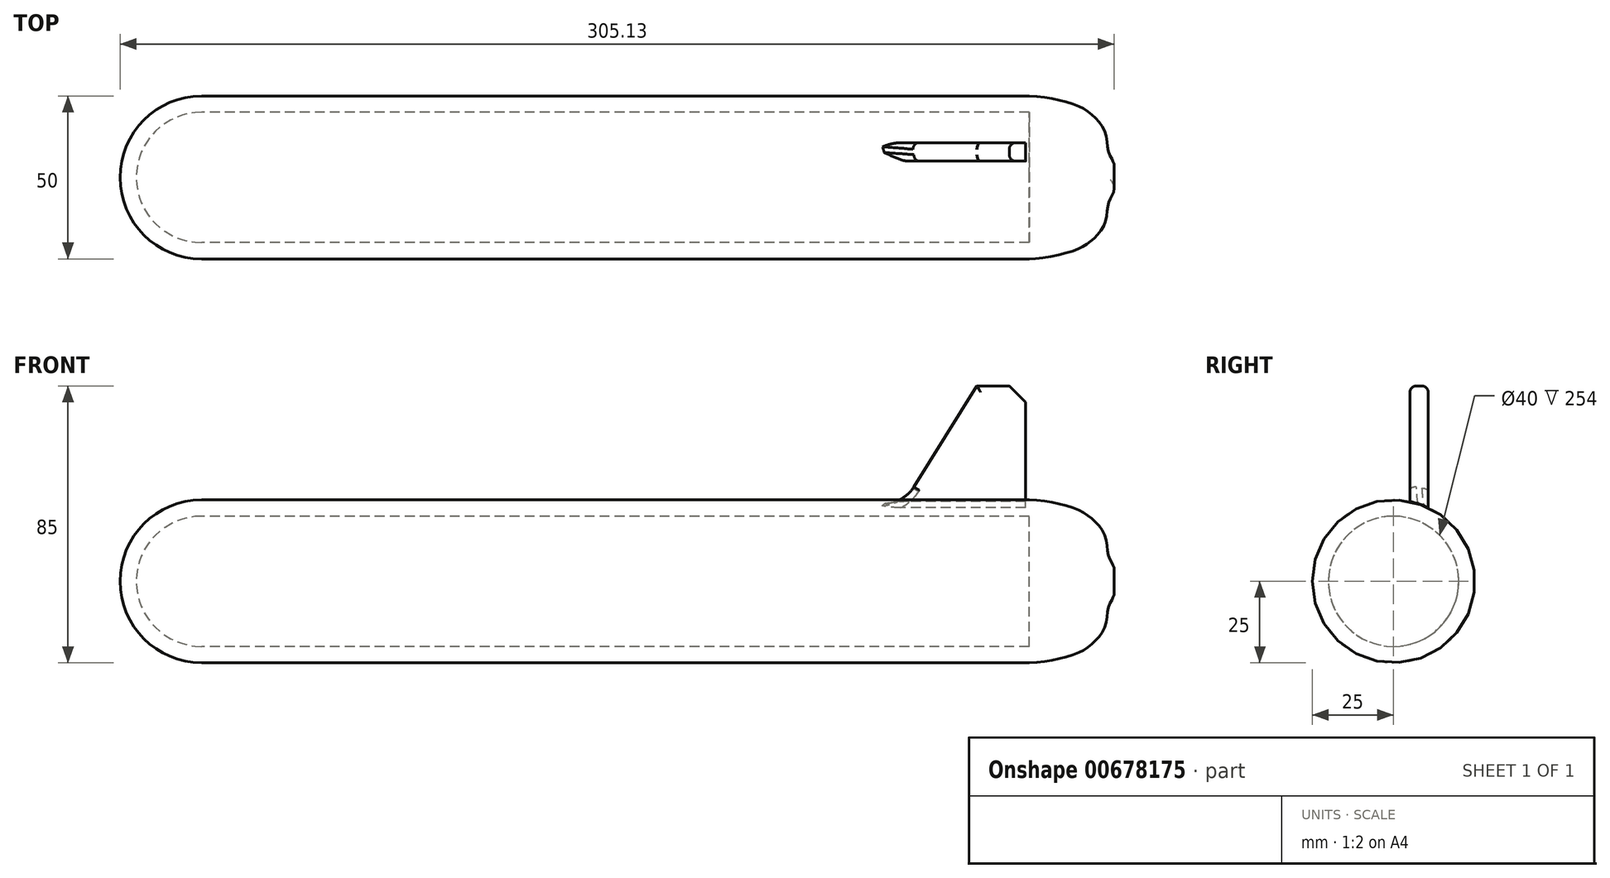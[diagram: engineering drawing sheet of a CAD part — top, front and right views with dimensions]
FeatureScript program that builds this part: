
annotation { "Feature Type Name" : "Feature", "Feature Type Description" : "" }
export const myFeature = defineFeature(function(context is Context, id is Id, definition is map)
    precondition{}
    {
        {
            var Q0;
            Q0=qCreatedBy(makeId("Right.planeOp"),FACE);
            var sketch = newSketch(context, id + "F0", { "sketchPlane" : qUnion([Q0])});
            skCircle(sketch, "E0", {"center": v(0, 0) * mm, "radius": 25 * mm});
            skCircle(sketch, "E1", {"center": v(0, 0) * mm, "radius": 20 * mm});
            skSolve(sketch);
        }
        {
            var Q0;
            Q0=makeQuery(id+"F0.imprint","IMPRINT",FACE,{"disambiguationData":[TD([[makeQuery(id+"F0.imprint","IMPRINT",EDGE,{"derivedFrom":sQuery(id+"F0.wireOp",EDGE,"E0")}),1.0]])]});
            extrude(context, id + "F1", {"entities" : qUnion([Q0]), "endBound" : BoundingType.SYMMETRIC, "depth" : 254 * mm, "offsetDistance" : 25 * mm});
        }
        {
            var Q0;
            Q0=makeQuery(id+"F1.opExtrude","CAP_FACE",FACE,{"disambiguationData":[OSD([sQuery(id+"F0.wireOp",EDGE,"E0"),sQuery(id+"F0.wireOp",EDGE,"E1")])],"isStart":true});
            var sketch = newSketch(context, id + "F2", { "sketchPlane" : qUnion([Q0])});
            skLineSegment(sketch, "E2", {"start": v(0, 46.44) * mm, "end": v(0, -46.44) * mm, "construction": true});
            skArc(sketch, "E3", {"start": v(0, -25) * mm, "mid": v(25, 0) * mm, "end": v(0, 25) * mm});
            skArc(sketch, "E4", {"start": v(0, -20) * mm, "mid": v(20, 0) * mm, "end": v(0, 20) * mm});
            skLineSegment(sketch, "E5", {"start": v(0, 25) * mm, "end": v(0, 20) * mm});
            skLineSegment(sketch, "E6", {"start": v(0, -20) * mm, "end": v(0, -25) * mm});
            skSolve(sketch);
        }
        {
            var Q0;
            Q0=makeQuery(id+"F2.imprint","IMPRINT",FACE,{"disambiguationData":[TD([[makeQuery(id+"F2.imprint","IMPRINT",EDGE,{"derivedFrom":sQuery(id+"F2.wireOp",EDGE,"E3")}),-1.0]])]});
            var Q1;
            Q1=sQuery(id+"F2.wireOp",EDGE,"E2");
            revolve(context, id + "F3", {"operationType" : NewBodyOperationType.ADD, "entities" : qUnion([Q0]), "axis" : qUnion([Q1]), "revolveType" : RevolveType.ONE_DIRECTION, "angle" : 180 * degree});
        }
        {
            var Q0;
            Q0=qCreatedBy(makeId("Top.planeOp"),FACE);
            var sketch = newSketch(context, id + "F4", { "sketchPlane" : qUnion([Q0])});
            skFitSpline(sketch, "E7.MirrorCS", {"points": [v(127, -25) * mm, v(140.66, -22.5) * mm, v(146.09, -19.4) * mm, v(150.23, -14.19) * mm, v(151.3, -8.12) * mm, v(152.86, -4.69) * mm, v(151.36, 0) * mm], "startDerivative": vector(46.37, -0.27) * mm, "endDerivative": vector(-41.82, 42.97) * mm});
            skLineSegment(sketch, "E8", {"start": v(0, 0) * mm, "end": v(187.94, 0) * mm, "construction": true});
            skLineSegment(sketch, "E9", {"start": v(151.36, 0) * mm, "end": v(127, 0) * mm});
            skLineSegment(sketch, "E10", {"start": v(127, -25) * mm, "end": v(127, 0) * mm});
            skSolve(sketch);
        }
        {
            var Q0;
            Q0=makeQuery(id+"F4.imprint","IMPRINT",FACE,{"disambiguationData":[TD([[makeQuery(id+"F4.imprint","IMPRINT",EDGE,{"derivedFrom":sQuery(id+"F4.wireOp",EDGE,"E7.MirrorCS")}),1.0]])]});
            var Q1;
            Q1=sQuery(id+"F4.wireOp",EDGE,"E8");
            revolve(context, id + "F5", {"operationType" : NewBodyOperationType.ADD, "entities" : qUnion([Q0]), "axis" : qUnion([Q1]), "revolveType" : RevolveType.FULL});
        }
        {
            var Q0;
            Q0=qCreatedBy(makeId("Top.planeOp"),FACE);
            cPlane(context, id + "F6", {"entities" : qUnion([Q0]), "cplaneType" : CPlaneType.OFFSET, "offset" : 60 * mm, "width" : 150 * mm, "height" : 150 * mm});
        }
        {
            var Q0;
            Q0=qCreatedBy(id+"F6.planeOp",FACE);
            var sketch = newSketch(context, id + "F7", { "sketchPlane" : qUnion([Q0])});
            skLineSegment(sketch, "E11.bottom", {"start": v(125.91, 5) * mm, "end": v(86, 5) * mm});
            skLineSegment(sketch, "E11.top", {"start": v(125.91, 10.65) * mm, "end": v(86, 10.65) * mm});
            skLineSegment(sketch, "E11.left", {"start": v(125.91, 5) * mm, "end": v(125.91, 10.65) * mm});
            skLineSegment(sketch, "E11.right", {"start": v(86, 5) * mm, "end": v(86, 10.65) * mm});
            skPoint(sketch, "E11.middle", {"position": v(105.96, 7.82) * mm});
            skSolve(sketch);
        }
        {
            var Q0;
            Q0=makeQuery(id+"F7.imprint","IMPRINT",FACE,{"disambiguationData":[TD([[makeQuery(id+"F7.imprint","IMPRINT",EDGE,{"derivedFrom":sQuery(id+"F7.wireOp",EDGE,"E11.bottom")}),-1.0]])]});
            var Q1;
            Q1=makeQuery(id+"F1.opExtrude","SWEPT_FACE",FACE,{"disambiguationData":[OSD([sQuery(id+"F0.wireOp",EDGE,"E0")])]});
            extrude(context, id + "F8", {"entities" : qUnion([Q0]), "operationType" : NewBodyOperationType.ADD, "endBound" : BoundingType.UP_TO_SURFACE, "oppositeDirection" : true, "depth" : 25 * mm, "endBoundEntityFace" : qUnion([Q1]), "offsetDistance" : 25 * mm});
        }
        {
            var Q0;
            Q0=makeQuery(id+"F8.opExtrude","CAP_EDGE",EDGE,{"disambiguationData":[OSD([sQuery(id+"F7.wireOp",EDGE,"E11.left")])],"isStart":true});
            chamfer(context, id + "F9", {"entities" : qUnion([Q0]), "width" : 5 * mm, "tangentPropagation" : true});
        }
        {
            var Q0;
            Q0=makeQuery(id+"F8.opExtrude","CAP_EDGE",EDGE,{"disambiguationData":[OSD([sQuery(id+"F7.wireOp",EDGE,"E11.right")])],"isStart":true});
            chamfer(context, id + "F10", {"entities" : qUnion([Q0]), "chamferType" : ChamferType.TWO_OFFSETS, "width1" : 40 * mm, "oppositeDirection" : false, "width2" : 25 * mm, "tangentPropagation" : true});
        }
        {
            var Q0;
            {var subQ0=sQuery(id+"F7.wireOp",EDGE,"E11.right");Q0=makeQuery(id+"F10.opChamfer","BLEND_EDGE",EDGE,{"blendedFrom":[makeQuery(id+"F8.opExtrude","CAP_EDGE",EDGE,{"disambiguationData":[OSD([subQ0])],"isStart":true}),makeQuery(id+"F8.opExtrude","CAP_FACE",FACE,{"disambiguationData":[OSD([sQuery(id+"F7.wireOp",EDGE,"E11.bottom"),sQuery(id+"F7.wireOp",EDGE,"E11.top"),sQuery(id+"F7.wireOp",EDGE,"E11.left"),subQ0])],"isStart":true})],"blendedInto":[makeQuery(id+"F8.opExtrude","CAP_FACE",FACE,{"disambiguationData":[OSD([sQuery(id+"F7.wireOp",EDGE,"E11.bottom"),sQuery(id+"F7.wireOp",EDGE,"E11.top"),sQuery(id+"F7.wireOp",EDGE,"E11.left"),subQ0])],"isStart":true})]});}
            var Q1;
            {var subQ0=sQuery(id+"F7.wireOp",EDGE,"E11.left");Q1=makeQuery(id+"F9.opChamfer","BLEND_EDGE",EDGE,{"blendedFrom":[makeQuery(id+"F8.opExtrude","CAP_EDGE",EDGE,{"disambiguationData":[OSD([subQ0])],"isStart":true}),makeQuery(id+"F8.opExtrude","SWEPT_FACE",FACE,{"disambiguationData":[OSD([subQ0])]})],"blendedInto":[makeQuery(id+"F8.opExtrude","SWEPT_FACE",FACE,{"disambiguationData":[OSD([subQ0])]})]});}
            fillet(context, id + "F11", {"entities" : qUnion([Q0, Q1]), "radius" : 0.12 * mm, "tangentPropagation" : true, "defaultsChanged" : false, "vertexSettings" : [], "allowEdgeOverflow" : false});
        }
        {
            var Q0;
            Q0=makeQuery(id+"F10.opChamfer","BLEND_EDGE",EDGE,{"blendedFrom":[makeQuery(id+"F8.opExtrude","CAP_EDGE",EDGE,{"disambiguationData":[OSD([sQuery(id+"F7.wireOp",EDGE,"E11.right")])],"isStart":true}),makeQuery(id+"F1.opExtrude","SWEPT_FACE",FACE,{"disambiguationData":[OSD([sQuery(id+"F0.wireOp",EDGE,"E0")])]})],"blendedInto":[makeQuery(id+"F1.opExtrude","SWEPT_FACE",FACE,{"disambiguationData":[OSD([sQuery(id+"F0.wireOp",EDGE,"E0")])]})]});
            fillet(context, id + "F12", {"entities" : qUnion([Q0]), "radius" : 10 * mm, "tangentPropagation" : true, "allowEdgeOverflow" : false});
        }
        {
            var Q0;
            Q0=makeQuery(id+"F10.opChamfer","BLEND_EDGE",EDGE,{"blendedFrom":[makeQuery(id+"F8.opExtrude","CAP_EDGE",EDGE,{"disambiguationData":[OSD([sQuery(id+"F7.wireOp",EDGE,"E11.right")])],"isStart":true}),makeQuery(id+"F8.opExtrude","SWEPT_FACE",FACE,{"disambiguationData":[OSD([sQuery(id+"F7.wireOp",EDGE,"E11.top")])]})],"blendedInto":[makeQuery(id+"F8.opExtrude","SWEPT_FACE",FACE,{"disambiguationData":[OSD([sQuery(id+"F7.wireOp",EDGE,"E11.top")])]})]});
            var Q1;
            Q1=makeQuery(id+"F10.opChamfer","BLEND_EDGE",EDGE,{"blendedFrom":[makeQuery(id+"F8.opExtrude","CAP_EDGE",EDGE,{"disambiguationData":[OSD([sQuery(id+"F7.wireOp",EDGE,"E11.right")])],"isStart":true}),makeQuery(id+"F8.opExtrude","SWEPT_FACE",FACE,{"disambiguationData":[OSD([sQuery(id+"F7.wireOp",EDGE,"E11.bottom")])]})],"blendedInto":[makeQuery(id+"F8.opExtrude","SWEPT_FACE",FACE,{"disambiguationData":[OSD([sQuery(id+"F7.wireOp",EDGE,"E11.bottom")])]})]});
            fillet(context, id + "F13", {"entities" : qUnion([Q0, Q1]), "radius" : 2 * mm, "tangentPropagation" : true, "allowEdgeOverflow" : false});
        }
    });
